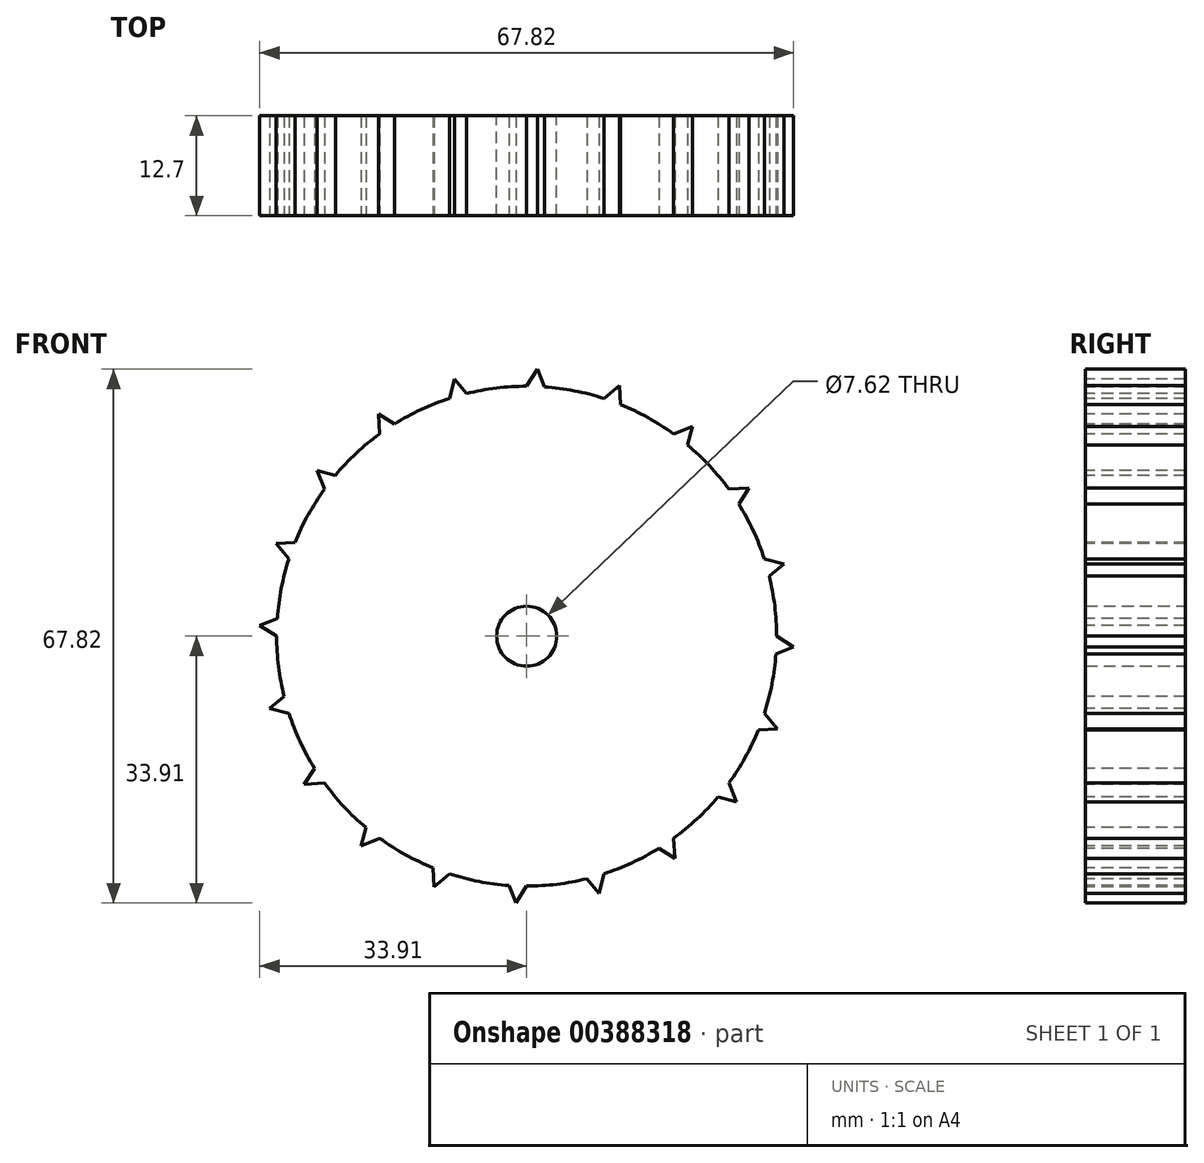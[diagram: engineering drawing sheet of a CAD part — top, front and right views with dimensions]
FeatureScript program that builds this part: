
annotation { "Feature Type Name" : "Feature", "Feature Type Description" : "" }
export const myFeature = defineFeature(function(context is Context, id is Id, definition is map)
    precondition{}
    {
        {
            var Q0;
            Q0=qCreatedBy(makeId("Front.planeOp"),FACE);
            var sketch = newSketch(context, id + "F0", { "sketchPlane" : qUnion([Q0])});
            skCircle(sketch, "E0", {"center": v(0, 0) * mm, "radius": 31.75 * mm});
            skCircle(sketch, "E1", {"center": v(0, 0) * mm, "radius": 3.81 * mm});
            skSolve(sketch);
        }
        {
            var Q0;
            Q0=makeQuery(id+"F0.imprint","IMPRINT",FACE,{"disambiguationData":[TD([[makeQuery(id+"F0.imprint","IMPRINT",EDGE,{"derivedFrom":sQuery(id+"F0.wireOp",EDGE,"E0")}),1.0]])]});
            extrude(context, id + "F1", {"entities" : qUnion([Q0]), "depth" : 12.7 * mm});
        }
        {
            var Q0;
            Q0=makeQuery(id+"F1.opExtrude","CAP_FACE",FACE,{"disambiguationData":[OSD([sQuery(id+"F0.wireOp",EDGE,"E0"),sQuery(id+"F0.wireOp",EDGE,"E1")])],"isStart":false});
            var sketch = newSketch(context, id + "F2", { "sketchPlane" : qUnion([Q0])});
            skLineSegment(sketch, "E2", {"start": v(0, 31.75) * mm, "end": v(1.38, 33.91) * mm});
            skLineSegment(sketch, "E3", {"start": v(1.38, 33.91) * mm, "end": v(2.24, 31.67) * mm});
            skSolve(sketch);
        }
        {
            var Q0;
            Q0=qCreatedBy(makeId("Top.planeOp"),FACE);
            var sketch = newSketch(context, id + "F3", { "sketchPlane" : qUnion([Q0])});
            skLineSegment(sketch, "E4", {"start": v(0, 6.68) * mm, "end": v(0, -22.56) * mm, "construction": true});
            skSolve(sketch);
        }
        {
            var Q0;
            {var subQ0=sQuery(id+"F2.wireOp",EDGE,"E2");Q0=makeQuery(id+"F2.imprint","IMPRINT",FACE,{"disambiguationData":[TD([[makeQuery(id+"F2.imprint","IMPRINT",EDGE,{"derivedFrom":subQ0}),-1.0]])]});}
            var Q1;
            Q1=makeQuery(id+"F1.opExtrude","CAP_FACE",FACE,{"disambiguationData":[OSD([sQuery(id+"F0.wireOp",EDGE,"E0"),sQuery(id+"F0.wireOp",EDGE,"E1")])],"isStart":true});
            extrude(context, id + "F4", {"entities" : qUnion([Q0]), "endBound" : BoundingType.UP_TO_SURFACE, "oppositeDirection" : true, "endBoundEntityFace" : qUnion([Q1]), "depth" : 12.43 * mm});
        }
        {
            var Q0;
            Q0=makeQuery(id+"F4.opExtrude","SWEPT_BODY",BODY,{"disambiguationData":[OSD([sQuery(id+"F0.wireOp",EDGE,"E0"),sQuery(id+"F2.wireOp",EDGE,"E2"),sQuery(id+"F2.wireOp",EDGE,"E3")])]});
            var Q1;
            Q1=sQuery(id+"F3.wireOp",EDGE,"E4");
            circularPattern(context, id + "F5", {"operationType" : NewBodyOperationType.ADD, "entities" : qUnion([Q0]), "axis" : qUnion([Q1]), "angle" : 360 * degree, "instanceCount" : 20, "equalSpace" : true});
        }
    });
